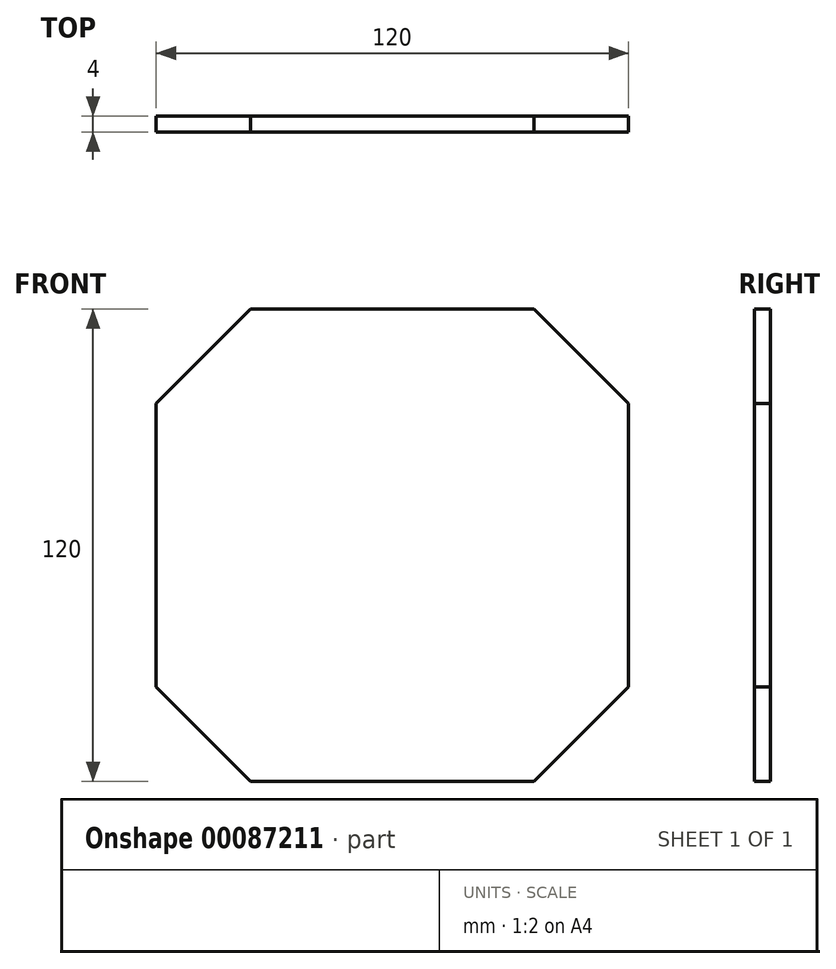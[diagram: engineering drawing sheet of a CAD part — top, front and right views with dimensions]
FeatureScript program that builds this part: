
annotation { "Feature Type Name" : "Feature", "Feature Type Description" : "" }
export const myFeature = defineFeature(function(context is Context, id is Id, definition is map)
    precondition{}
    {
        {
            var Q0;
            Q0=qCreatedBy(makeId("Front.planeOp"),FACE);
            var sketch = newSketch(context, id + "F0", { "sketchPlane" : qUnion([Q0])});
            skLineSegment(sketch, "E0.bottom", {"start": v(39.25, 91.53) * mm, "end": v(-32.67, 91.53) * mm});
            skLineSegment(sketch, "E0.top", {"start": v(39.25, -28.47) * mm, "end": v(-32.67, -28.47) * mm});
            skLineSegment(sketch, "E0.left", {"start": v(63.29, 67.49) * mm, "end": v(63.29, -4.43) * mm});
            skLineSegment(sketch, "E0.right", {"start": v(-56.71, 67.49) * mm, "end": v(-56.71, -4.43) * mm});
            skLineSegment(sketch, "E1", {"start": v(-32.67, 91.53) * mm, "end": v(-56.71, 67.49) * mm});
            skLineSegment(sketch, "E2", {"start": v(39.25, 91.53) * mm, "end": v(63.29, 67.49) * mm});
            skLineSegment(sketch, "E3", {"start": v(39.25, -28.47) * mm, "end": v(63.29, -4.43) * mm});
            skLineSegment(sketch, "E4", {"start": v(-32.67, -28.47) * mm, "end": v(-56.71, -4.43) * mm});
            skPoint(sketch, "E5.orphan", {"position": v(-56.71, 91.53) * mm});
            skPoint(sketch, "E6.orphan", {"position": v(63.29, 91.53) * mm});
            skPoint(sketch, "E7.orphan", {"position": v(63.29, -28.47) * mm});
            skPoint(sketch, "E8.orphan", {"position": v(-56.71, -28.47) * mm});
            skPoint(sketch, "E9.start.orphan", {"position": v(33.29, 61.53) * mm});
            skPoint(sketch, "E10.end.orphan", {"position": v(-26.71, 61.53) * mm});
            skPoint(sketch, "E11.start.orphan", {"position": v(-26.71, 1.53) * mm});
            skPoint(sketch, "E12.start.orphan", {"position": v(33.29, 1.53) * mm});
            skPoint(sketch, "E13.end.orphan", {"position": v(63.29, 31.53) * mm});
            skPoint(sketch, "E14.orphan", {"position": v(3.29, 91.53) * mm});
            skPoint(sketch, "E15.orphan", {"position": v(-56.71, 31.53) * mm});
            skPoint(sketch, "E16.end.orphan", {"position": v(3.29, -28.47) * mm});
            skSolve(sketch);
        }
        {
            var Q0;
            Q0 = qSketchRegion(id + "F0", true);
            extrude(context, id + "F1", {"entities" : qUnion([Q0]), "depth" : 4 * mm});
        }
    });
